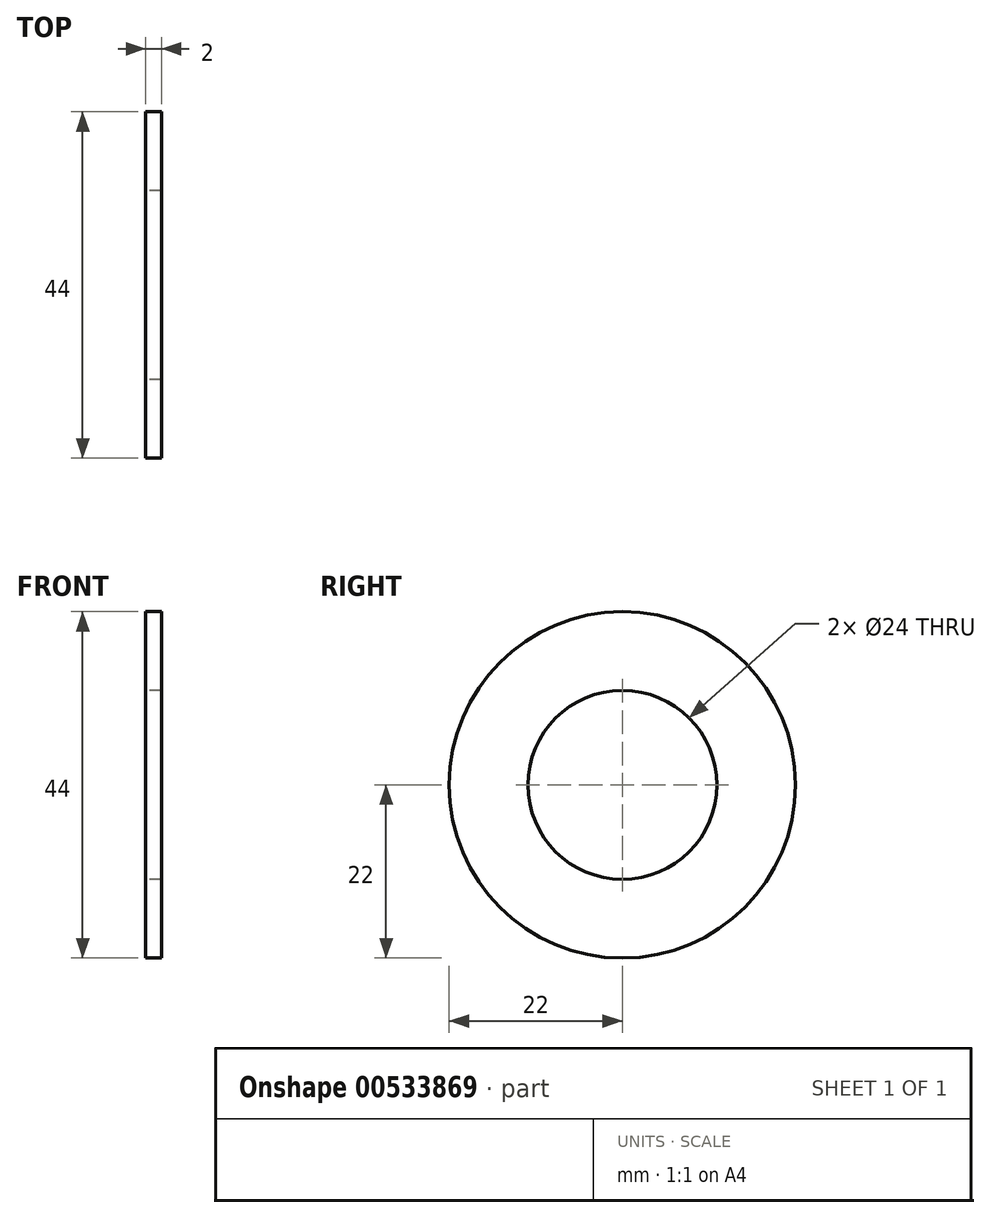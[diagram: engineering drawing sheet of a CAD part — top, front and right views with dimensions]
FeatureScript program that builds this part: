
annotation { "Feature Type Name" : "Feature", "Feature Type Description" : "" }
export const myFeature = defineFeature(function(context is Context, id is Id, definition is map)
    precondition{}
    {
        {
            var Q0;
            Q0=qCreatedBy(makeId("Right.planeOp"),FACE);
            var sketch = newSketch(context, id + "F0", { "sketchPlane" : qUnion([Q0])});
            skCircle(sketch, "E0", {"center": v(0, 0) * mm, "radius": 22 * mm});
            skCircle(sketch, "E1", {"center": v(0, 0) * mm, "radius": 12 * mm});
            skSolve(sketch);
        }
        {
            var Q0;
            Q0=makeQuery(id+"F0.imprint","IMPRINT",FACE,{"disambiguationData":[TD([[makeQuery(id+"F0.imprint","IMPRINT",EDGE,{"derivedFrom":sQuery(id+"F0.wireOp",EDGE,"E0")}),1.0]])]});
            extrude(context, id + "F1", {"entities" : qUnion([Q0]), "depth" : 2 * mm, "offsetDistance" : 25 * mm});
        }
    });
